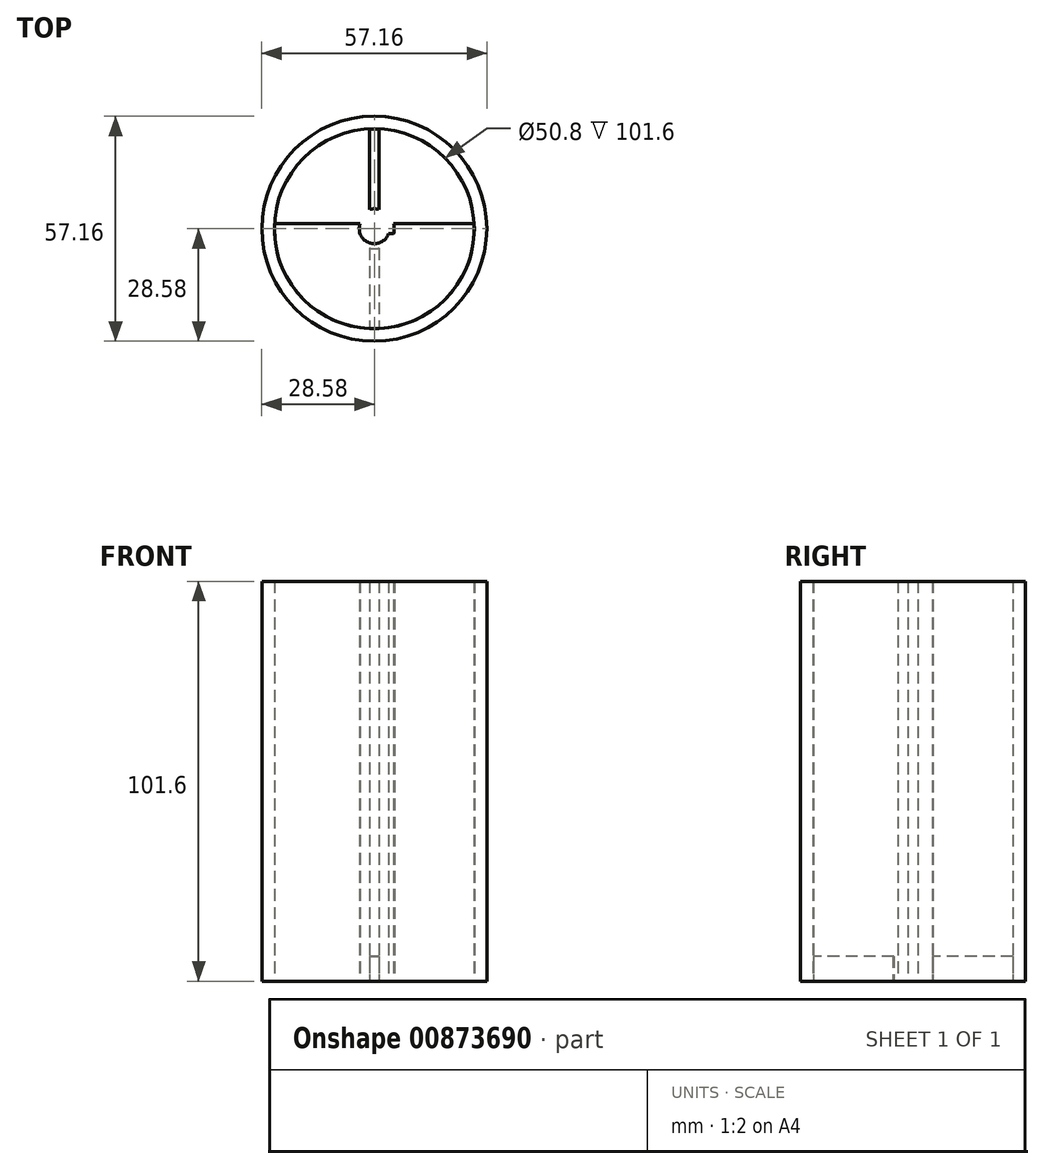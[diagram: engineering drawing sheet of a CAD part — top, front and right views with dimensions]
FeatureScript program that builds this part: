
annotation { "Feature Type Name" : "Feature", "Feature Type Description" : "" }
export const myFeature = defineFeature(function(context is Context, id is Id, definition is map)
    precondition{}
    {
        {
            var Q0;
            Q0=qCreatedBy(makeId("Top.planeOp"),FACE);
            var sketch = newSketch(context, id + "F0", { "sketchPlane" : qUnion([Q0])});
            skCircle(sketch, "E0", {"center": v(0, 0) * mm, "radius": 28.58 * mm});
            skCircle(sketch, "E1", {"center": v(0, 0) * mm, "radius": 25.4 * mm});
            skLineSegment(sketch, "E2.bottom", {"start": v(1.27, 25.37) * mm, "end": v(-1.27, 25.37) * mm});
            skLineSegment(sketch, "E2.top", {"start": v(1.27, -25.37) * mm, "end": v(-1.27, -25.37) * mm});
            skLineSegment(sketch, "E2.left", {"start": v(1.27, 25.37) * mm, "end": v(1.27, -25.37) * mm});
            skLineSegment(sketch, "E2.right", {"start": v(-1.27, 25.37) * mm, "end": v(-1.27, -25.37) * mm});
            skLineSegment(sketch, "E3.bottom", {"start": v(25.37, -1.27) * mm, "end": v(-25.37, -1.27) * mm});
            skLineSegment(sketch, "E3.top", {"start": v(25.37, 1.27) * mm, "end": v(-25.37, 1.27) * mm});
            skLineSegment(sketch, "E3.left", {"start": v(25.37, -1.27) * mm, "end": v(25.37, 1.27) * mm});
            skLineSegment(sketch, "E3.right", {"start": v(-25.37, -1.27) * mm, "end": v(-25.37, 1.27) * mm});
            skCircle(sketch, "E4", {"center": v(0, 0) * mm, "radius": 3.81 * mm});
            skCircle(sketch, "E5", {"center": v(0, 0) * mm, "radius": 5.08 * mm});
            skSolve(sketch);
        }
        {
            var Q0;
            Q0=makeQuery(id+"F0.imprint","IMPRINT",FACE,{"disambiguationData":[TD([[makeQuery(id+"F0.imprint","IMPRINT",EDGE,{"derivedFrom":sQuery(id+"F0.wireOp",EDGE,"E0")}),1.0]])]});
            extrude(context, id + "F1", {"entities" : qUnion([Q0]), "depth" : 101.6 * mm, "offsetDistance" : 25.4 * mm});
        }
        {
            var Q0;
            {var subQ0=sQuery(id+"F0.wireOp",EDGE,"E3.left");Q0=makeQuery(id+"F0.imprint","IMPRINT",FACE,{"disambiguationData":[TD([[makeQuery(id+"F0.imprint","IMPRINT",EDGE,{"derivedFrom":subQ0}),1.0]])]});}
            var Q1;
            {var subQ0=sQuery(id+"F0.wireOp",EDGE,"E2.top");Q1=makeQuery(id+"F0.imprint","IMPRINT",FACE,{"disambiguationData":[TD([[makeQuery(id+"F0.imprint","IMPRINT",EDGE,{"derivedFrom":subQ0}),-1.0]])]});}
            var Q2;
            {var subQ0=sQuery(id+"F0.wireOp",EDGE,"E3.right");Q2=makeQuery(id+"F0.imprint","IMPRINT",FACE,{"disambiguationData":[TD([[makeQuery(id+"F0.imprint","IMPRINT",EDGE,{"derivedFrom":subQ0}),-1.0]])]});}
            var Q3;
            {var subQ0=sQuery(id+"F0.wireOp",EDGE,"E2.bottom");Q3=makeQuery(id+"F0.imprint","IMPRINT",FACE,{"disambiguationData":[TD([[makeQuery(id+"F0.imprint","IMPRINT",EDGE,{"derivedFrom":subQ0}),1.0]])]});}
            var Q4;
            {var subQ0=sQuery(id+"F0.wireOp",EDGE,"E4");var subQ1=sQuery(id+"F0.wireOp",EDGE,"E2.left");var subQ2=makeQuery(id+"F0.imprint","INTERSECT",VERTEX,{"disambiguationData":[OD(1.0)],"derivedFrom":[subQ1,subQ0]});Q4=makeQuery(id+"F0.imprint","IMPRINT",FACE,{"disambiguationData":[TD([[makeQuery(id+"F0.imprint","IMPRINT",EDGE,{"disambiguationData":[TD([[subQ2,-1.0]])],"derivedFrom":subQ1}),1.0]])]});}
            var Q5;
            {var subQ0=sQuery(id+"F0.wireOp",EDGE,"E5");var subQ1=sQuery(id+"F0.wireOp",EDGE,"E3.bottom");var subQ2=makeQuery(id+"F0.imprint","INTERSECT",VERTEX,{"disambiguationData":[OD(0.0)],"derivedFrom":[subQ1,subQ0]});Q5=makeQuery(id+"F0.imprint","IMPRINT",FACE,{"disambiguationData":[TD([[makeQuery(id+"F0.imprint","IMPRINT",EDGE,{"disambiguationData":[TD([[subQ2,-1.0]])],"derivedFrom":subQ1}),-1.0]])]});}
            var Q6;
            {var subQ0=sQuery(id+"F0.wireOp",EDGE,"E5");var subQ1=sQuery(id+"F0.wireOp",EDGE,"E2.left");var subQ2=makeQuery(id+"F0.imprint","INTERSECT",VERTEX,{"disambiguationData":[OD(0.0)],"derivedFrom":[subQ1,subQ0]});Q6=makeQuery(id+"F0.imprint","IMPRINT",FACE,{"disambiguationData":[TD([[makeQuery(id+"F0.imprint","IMPRINT",EDGE,{"disambiguationData":[TD([[subQ2,-1.0]])],"derivedFrom":subQ1}),1.0]])]});}
            var Q7;
            {var subQ0=sQuery(id+"F0.wireOp",EDGE,"E5");var subQ1=sQuery(id+"F0.wireOp",EDGE,"E2.left");var subQ2=makeQuery(id+"F0.imprint","INTERSECT",VERTEX,{"disambiguationData":[OD(0.0)],"derivedFrom":[subQ1,subQ0]});Q7=makeQuery(id+"F0.imprint","IMPRINT",FACE,{"disambiguationData":[TD([[makeQuery(id+"F0.imprint","IMPRINT",EDGE,{"disambiguationData":[TD([[subQ2,-1.0]])],"derivedFrom":subQ1}),-1.0]])]});}
            var Q8;
            {var subQ0=sQuery(id+"F0.wireOp",EDGE,"E5");var subQ1=sQuery(id+"F0.wireOp",EDGE,"E2.right");var subQ2=makeQuery(id+"F0.imprint","INTERSECT",VERTEX,{"disambiguationData":[OD(0.0)],"derivedFrom":[subQ1,subQ0]});Q8=makeQuery(id+"F0.imprint","IMPRINT",FACE,{"disambiguationData":[TD([[makeQuery(id+"F0.imprint","IMPRINT",EDGE,{"disambiguationData":[TD([[subQ2,-1.0]])],"derivedFrom":subQ1}),-1.0]])]});}
            var Q9;
            {var subQ0=sQuery(id+"F0.wireOp",EDGE,"E4");var subQ1=sQuery(id+"F0.wireOp",EDGE,"E3.bottom");var subQ2=makeQuery(id+"F0.imprint","INTERSECT",VERTEX,{"disambiguationData":[OD(1.0)],"derivedFrom":[subQ1,subQ0]});Q9=makeQuery(id+"F0.imprint","IMPRINT",FACE,{"disambiguationData":[TD([[makeQuery(id+"F0.imprint","IMPRINT",EDGE,{"disambiguationData":[TD([[subQ2,-1.0]])],"derivedFrom":subQ1}),-1.0]])]});}
            var Q10;
            {var subQ0=sQuery(id+"F0.wireOp",EDGE,"E4");var subQ1=sQuery(id+"F0.wireOp",EDGE,"E2.right");var subQ2=makeQuery(id+"F0.imprint","INTERSECT",VERTEX,{"disambiguationData":[OD(1.0)],"derivedFrom":[subQ1,subQ0]});Q10=makeQuery(id+"F0.imprint","IMPRINT",FACE,{"disambiguationData":[TD([[makeQuery(id+"F0.imprint","IMPRINT",EDGE,{"disambiguationData":[TD([[subQ2,-1.0]])],"derivedFrom":subQ1}),-1.0]])]});}
            var Q11;
            {var subQ0=sQuery(id+"F0.wireOp",EDGE,"E4");var subQ1=sQuery(id+"F0.wireOp",EDGE,"E2.left");var subQ2=makeQuery(id+"F0.imprint","INTERSECT",VERTEX,{"disambiguationData":[OD(1.0)],"derivedFrom":[subQ1,subQ0]});Q11=makeQuery(id+"F0.imprint","IMPRINT",FACE,{"disambiguationData":[TD([[makeQuery(id+"F0.imprint","IMPRINT",EDGE,{"disambiguationData":[TD([[subQ2,-1.0]])],"derivedFrom":subQ1}),-1.0]])]});}
            extrude(context, id + "F2", {"entities" : qUnion([Q0, Q1, Q2, Q3, Q4, Q5, Q6, Q7, Q8, Q9, Q10, Q11]), "depth" : 101.6 * mm, "offsetDistance" : 25.4 * mm});
        }
        {
            var Q0;
            {var subQ0=sQuery(id+"F0.wireOp",EDGE,"E2.left");var subQ5=sQuery(id+"F0.wireOp",EDGE,"E5");var subQ6=makeQuery(id+"F0.imprint","INTERSECT",VERTEX,{"disambiguationData":[OD(0.0)],"derivedFrom":[subQ0,subQ5]});Q0=makeQuery(id+"F0.imprint","IMPRINT",FACE,{"disambiguationData":[TD([[makeQuery(id+"F0.imprint","IMPRINT",EDGE,{"disambiguationData":[TD([[subQ6,1.0]])],"derivedFrom":subQ5}),-1.0]])]});}
            var Q1;
            {var subQ0=sQuery(id+"F0.wireOp",EDGE,"E2.right");var subQ5=sQuery(id+"F0.wireOp",EDGE,"E5");var subQ6=makeQuery(id+"F0.imprint","INTERSECT",VERTEX,{"disambiguationData":[OD(0.0)],"derivedFrom":[subQ0,subQ5]});Q1=makeQuery(id+"F0.imprint","IMPRINT",FACE,{"disambiguationData":[TD([[makeQuery(id+"F0.imprint","IMPRINT",EDGE,{"disambiguationData":[TD([[subQ6,-1.0]])],"derivedFrom":subQ5}),-1.0]])]});}
            var Q2;
            {var subQ0=sQuery(id+"F0.wireOp",EDGE,"E2.right");var subQ5=sQuery(id+"F0.wireOp",EDGE,"E5");var subQ6=makeQuery(id+"F0.imprint","INTERSECT",VERTEX,{"disambiguationData":[OD(1.0)],"derivedFrom":[subQ0,subQ5]});Q2=makeQuery(id+"F0.imprint","IMPRINT",FACE,{"disambiguationData":[TD([[makeQuery(id+"F0.imprint","IMPRINT",EDGE,{"disambiguationData":[TD([[subQ6,1.0]])],"derivedFrom":subQ5}),-1.0]])]});}
            var Q3;
            {var subQ0=sQuery(id+"F0.wireOp",EDGE,"E2.left");var subQ5=sQuery(id+"F0.wireOp",EDGE,"E5");var subQ6=makeQuery(id+"F0.imprint","INTERSECT",VERTEX,{"disambiguationData":[OD(1.0)],"derivedFrom":[subQ0,subQ5]});Q3=makeQuery(id+"F0.imprint","IMPRINT",FACE,{"disambiguationData":[TD([[makeQuery(id+"F0.imprint","IMPRINT",EDGE,{"disambiguationData":[TD([[subQ6,-1.0]])],"derivedFrom":subQ5}),-1.0]])]});}
            extrude(context, id + "F3", {"entities" : qUnion([Q0, Q1, Q2, Q3]), "depth" : 6.35 * mm, "offsetDistance" : 25.4 * mm});
        }
    });
